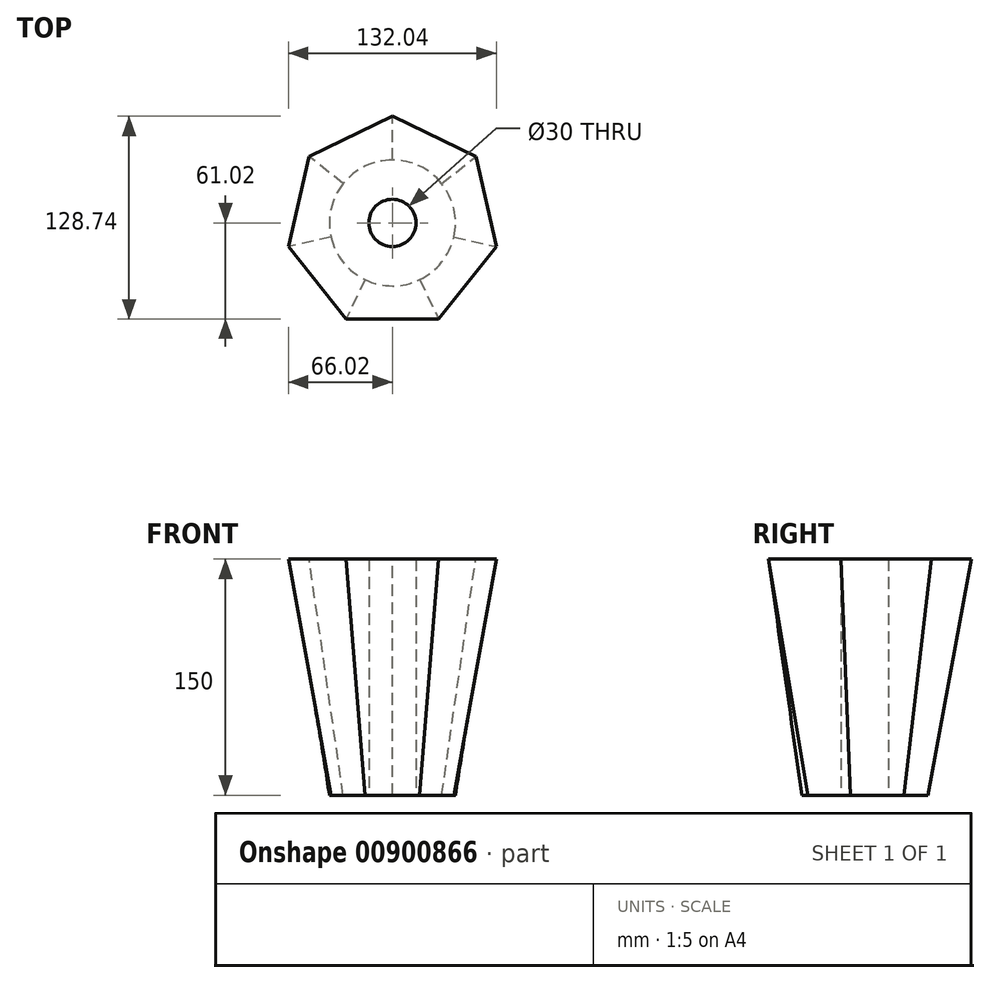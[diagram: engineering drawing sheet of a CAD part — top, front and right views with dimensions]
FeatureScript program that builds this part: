
annotation { "Feature Type Name" : "Feature", "Feature Type Description" : "" }
export const myFeature = defineFeature(function(context is Context, id is Id, definition is map)
    precondition{}
    {
        {
            var Q0;
            Q0=qCreatedBy(makeId("Top.planeOp"),FACE);
            cPlane(context, id + "F0", {"entities" : qUnion([Q0]), "cplaneType" : CPlaneType.OFFSET, "offset" : 150 * mm, "width" : 150 * mm, "height" : 150 * mm});
        }
        {
            var Q0;
            Q0=qCreatedBy(makeId("Top.planeOp"),FACE);
            var sketch = newSketch(context, id + "F1", { "sketchPlane" : qUnion([Q0])});
            skCircle(sketch, "E0", {"center": v(0, 0) * mm, "radius": 40 * mm});
            skSolve(sketch);
        }
        {
            var Q0;
            Q0=qCreatedBy(id+"F0.planeOp",FACE);
            var sketch = newSketch(context, id + "F2", { "sketchPlane" : qUnion([Q0])});
            skCircle(sketch, "E1.cCircle", {"center": v(0, 0) * mm, "radius": 67.72 * mm, "construction": true});
            skLineSegment(sketch, "E1.0", {"start": v(0, 67.72) * mm, "end": v(52.95, 42.22) * mm});
            skLineSegment(sketch, "E1.1", {"start": v(52.95, 42.22) * mm, "end": v(66.02, -15.07) * mm});
            skLineSegment(sketch, "E1.2", {"start": v(66.02, -15.07) * mm, "end": v(29.38, -61.02) * mm});
            skLineSegment(sketch, "E1.3", {"start": v(29.38, -61.02) * mm, "end": v(-29.38, -61.02) * mm});
            skLineSegment(sketch, "E1.4", {"start": v(-29.38, -61.02) * mm, "end": v(-66.02, -15.07) * mm});
            skLineSegment(sketch, "E1.5", {"start": v(-66.02, -15.07) * mm, "end": v(-52.95, 42.22) * mm});
            skLineSegment(sketch, "E1.6", {"start": v(-52.95, 42.22) * mm, "end": v(0, 67.72) * mm});
            skSolve(sketch);
        }
        {
            var Q0;
            Q0=makeQuery(id+"F1.imprint","IMPRINT",FACE,{"disambiguationData":[TD([[makeQuery(id+"F1.imprint","IMPRINT",EDGE,{"derivedFrom":sQuery(id+"F1.wireOp",EDGE,"E0")}),1.0]])]});
            var Q1;
            Q1=makeQuery(id+"F2.imprint","IMPRINT",FACE,{"disambiguationData":[TD([[makeQuery(id+"F2.imprint","IMPRINT",EDGE,{"derivedFrom":sQuery(id+"F2.wireOp",EDGE,"E1.0")}),-1.0]])]});
            loft(context, id + "F3", {"sheetProfilesArray" : [{ "sheetProfileEntities" : qUnion([Q0]) }, { "sheetProfileEntities" : qUnion([Q1]) }]});
        }
        {
            var Q0;
            Q0=makeQuery(id+"F3.opLoft","CAP_FACE",FACE,{"disambiguationData":[OSD([makeQuery(id+"F1.imprint","IMPRINT",FACE,{"disambiguationData":[TD([[makeQuery(id+"F1.imprint","IMPRINT",EDGE,{"derivedFrom":sQuery(id+"F1.wireOp",EDGE,"E0")}),1.0]])]})])],"isStart":true});
            var sketch = newSketch(context, id + "F4", { "sketchPlane" : qUnion([Q0])});
            skCircle(sketch, "E2", {"center": v(0, 0) * mm, "radius": 15 * mm});
            skSolve(sketch);
        }
        {
            var Q0;
            Q0 = qSketchRegion(id + "F4", true);
            extrude(context, id + "F5", {"entities" : qUnion([Q0]), "operationType" : NewBodyOperationType.REMOVE, "oppositeDirection" : true, "depth" : 172 * mm, "offsetDistance" : 25 * mm});
        }
    });
